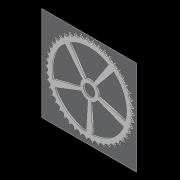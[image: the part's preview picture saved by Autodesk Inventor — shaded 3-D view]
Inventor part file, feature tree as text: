
AUTODESK INVENTOR PART (.ipt)
format: ipt  version: 2021 (Build 250183000, 183)  size: 968,704 bytes
history: native  units: mm
features: other x6, extrude x4, pattern_circular x2, sketch x2, pattern_linear x1, plane x1
ambient origin geometry x8: Origin, YZ Plane, XZ Plane, XY Plane, X Axis, Y Axis, Z Axis, Center Point
bodies: Solid1 (feature_tree)
feature tree (16):
  other  "Theoretical Tooth Profile"
  other  "Tooth Profile"
  other  "Section Profile"
  other  "Shroud"
  other  "Strand"
  pattern_linear  "Strand Pattern"  Spacing1=3.91375mm  [1 undecoded]
  extrude  "Theoretical Tooth"  Depth=10.0mm
  extrude  "Tooth"  Depth=10.0mm
  pattern_circular  "Tooth Pattern"  [2 undecoded]
  other  "Timing Plane"
  extrude  "Extrusion4"  Depth=10.11375mm
  pattern_circular  "Circular Pattern2"  [2 undecoded]
  plane  "Work Plane3"
  extrude  "Extrusion5"  Depth=10.0mm TaperAngle=0.0deg
  sketch  "Sketch4"  dims[d0=186.101273mm]
  sketch  "Sketch5"  dims[d2=1.36591mm d3=3.91375mm d10=22.044267mm d11=2.929118mm d12=6.2mm d13=10.11375mm d14=10.85mm d18=10.0mm d19=0.0mm d20=460.0mm d21=360.0deg d23=3.81mm d28=0.0mm d29=0.0mm d30=3.069mm d31=166.745028mm d32=3.069mm d33=0.762mm d34=12.7mm d36=90.0deg d37=90.0deg d38=10.0mm d40=13.92mm d42=0.0mm d43=1.5345mm d44=24.093133mm d45=44.64mm d46=3.91375mm d47=10.0mm d48=0.0mm d49=0.0mm d50=10.0mm d51=80.0mm d52=21.118484mm d53=10.821041mm d54=20.0mm d55=20.245819mm d56=8.901179mm d57=0.0mm d58=0.0mm d59=50.0mm d60=360.0deg d62=0.0mm d63=24.0mm d64=10.0mm d65=0.0mm]
note: 5 required parameter values undecoded (feature->parameter linkage not recoverable at this tier; creation-order binding heuristic only, values carry confidence <= 0.55)
